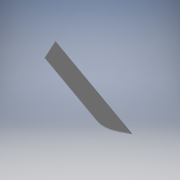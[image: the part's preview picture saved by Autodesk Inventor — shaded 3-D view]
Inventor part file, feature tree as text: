
AUTODESK INVENTOR PART (.ipt)
format: ipt  version: 2017 (Build 210142000, 142)  size: 145,920 bytes
history: native  units: mm
features: extrude x1, fillet x1
ambient origin geometry x8: Origin, YZ Plane, XZ Plane, XY Plane, X Axis, Y Axis, Z Axis, Center Point
bodies: Solid1 (feature_tree)
feature tree (2):
  extrude  "Extrusion1"  Depth=5.0mm TaperAngle=0.0deg
  fillet  "Fillet1"  Radius=153.25mm
